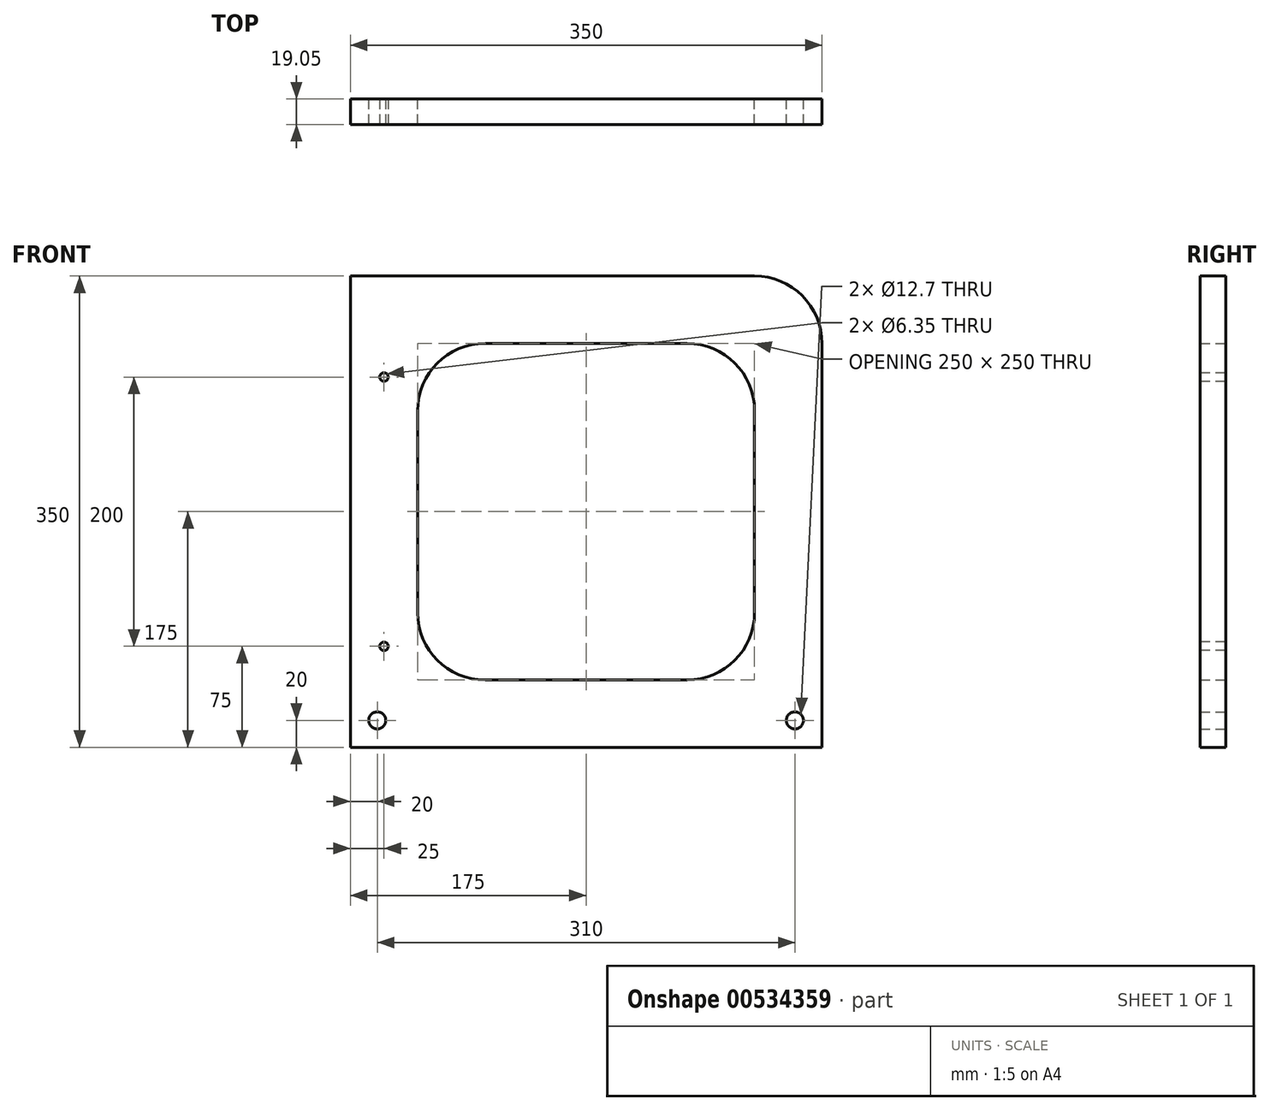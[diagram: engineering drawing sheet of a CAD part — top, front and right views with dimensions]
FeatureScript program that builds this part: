
annotation { "Feature Type Name" : "Feature", "Feature Type Description" : "" }
export const myFeature = defineFeature(function(context is Context, id is Id, definition is map)
    precondition{}
    {
        {
            var Q0;
            Q0=qCreatedBy(makeId("Front.planeOp"),FACE);
            var sketch = newSketch(context, id + "F0", { "sketchPlane" : qUnion([Q0])});
            skLineSegment(sketch, "E0.bottom", {"start": v(0, 0) * mm, "end": v(350, 0) * mm});
            skLineSegment(sketch, "E0.top", {"start": v(0, 350) * mm, "end": v(350, 350) * mm});
            skLineSegment(sketch, "E0.left", {"start": v(0, 0) * mm, "end": v(0, 350) * mm});
            skLineSegment(sketch, "E0.right", {"start": v(350, 0) * mm, "end": v(350, 350) * mm});
            skCircle(sketch, "E1", {"center": v(20, 20) * mm, "radius": 6.35 * mm});
            skCircle(sketch, "E2", {"center": v(330, 20) * mm, "radius": 6.35 * mm});
            skLineSegment(sketch, "E3.bottom", {"start": v(50, 300) * mm, "end": v(300, 300) * mm});
            skLineSegment(sketch, "E3.top", {"start": v(50, 50) * mm, "end": v(300, 50) * mm});
            skLineSegment(sketch, "E3.left", {"start": v(50, 300) * mm, "end": v(50, 50) * mm});
            skLineSegment(sketch, "E3.right", {"start": v(300, 300) * mm, "end": v(300, 50) * mm});
            skSolve(sketch);
        }
        {
            var Q0;
            Q0=makeQuery(id+"F0.imprint","IMPRINT",FACE,{"disambiguationData":[TD([[makeQuery(id+"F0.imprint","IMPRINT",EDGE,{"derivedFrom":sQuery(id+"F0.wireOp",EDGE,"E0.bottom")}),1.0]])]});
            extrude(context, id + "F1", {"entities" : qUnion([Q0]), "depth" : 19.05 * mm, "offsetDistance" : 25 * mm});
        }
        {
            var Q0;
            Q0=makeQuery(id+"F1.opExtrude","SWEPT_EDGE",EDGE,{"disambiguationData":[OSD([sQuery(id+"F0.wireOp",EDGE,"E3.top"),sQuery(id+"F0.wireOp",EDGE,"E3.right")])]});
            var Q1;
            Q1=makeQuery(id+"F1.opExtrude","SWEPT_EDGE",EDGE,{"disambiguationData":[OSD([sQuery(id+"F0.wireOp",EDGE,"E3.bottom"),sQuery(id+"F0.wireOp",EDGE,"E3.right")])]});
            var Q2;
            Q2=makeQuery(id+"F1.opExtrude","SWEPT_EDGE",EDGE,{"disambiguationData":[OSD([sQuery(id+"F0.wireOp",EDGE,"E3.bottom"),sQuery(id+"F0.wireOp",EDGE,"E3.left")])]});
            var Q3;
            Q3=makeQuery(id+"F1.opExtrude","SWEPT_EDGE",EDGE,{"disambiguationData":[OSD([sQuery(id+"F0.wireOp",EDGE,"E3.top"),sQuery(id+"F0.wireOp",EDGE,"E3.left")])]});
            var Q4;
            Q4=makeQuery(id+"F1.opExtrude","SWEPT_EDGE",EDGE,{"disambiguationData":[OSD([sQuery(id+"F0.wireOp",EDGE,"E0.top"),sQuery(id+"F0.wireOp",EDGE,"E0.right")])]});
            fillet(context, id + "F2", {"entities" : qUnion([Q0, Q1, Q2, Q3, Q4]), "radius" : 50 * mm, "tangentPropagation" : true, "allowEdgeOverflow" : false});
        }
        {
            var Q0;
            Q0=makeQuery(id+"F1.opExtrude","CAP_FACE",FACE,{"disambiguationData":[OSD([sQuery(id+"F0.wireOp",EDGE,"E0.bottom"),sQuery(id+"F0.wireOp",EDGE,"E0.top"),sQuery(id+"F0.wireOp",EDGE,"E0.left"),sQuery(id+"F0.wireOp",EDGE,"E0.right"),sQuery(id+"F0.wireOp",EDGE,"E1"),sQuery(id+"F0.wireOp",EDGE,"E2"),sQuery(id+"F0.wireOp",EDGE,"E3.bottom"),sQuery(id+"F0.wireOp",EDGE,"E3.top"),sQuery(id+"F0.wireOp",EDGE,"E3.left"),sQuery(id+"F0.wireOp",EDGE,"E3.right")])],"isStart":false});
            var sketch = newSketch(context, id + "F3", { "sketchPlane" : qUnion([Q0])});
            skCircle(sketch, "E4", {"center": v(25, 275) * mm, "radius": 3.17 * mm});
            skCircle(sketch, "E5", {"center": v(25, 75) * mm, "radius": 3.17 * mm});
            skSolve(sketch);
        }
        {
            var Q0;
            Q0=makeQuery(id+"F3.imprint","IMPRINT",FACE,{"disambiguationData":[TD([[makeQuery(id+"F3.imprint","IMPRINT",EDGE,{"derivedFrom":sQuery(id+"F3.wireOp",EDGE,"E4")}),1.0]])]});
            var Q1;
            Q1=makeQuery(id+"F3.imprint","IMPRINT",FACE,{"disambiguationData":[TD([[makeQuery(id+"F3.imprint","IMPRINT",EDGE,{"derivedFrom":sQuery(id+"F3.wireOp",EDGE,"E5")}),1.0]])]});
            extrude(context, id + "F4", {"entities" : qUnion([Q0, Q1]), "operationType" : NewBodyOperationType.REMOVE, "oppositeDirection" : true, "depth" : 25 * mm, "offsetDistance" : 25 * mm});
        }
    });
